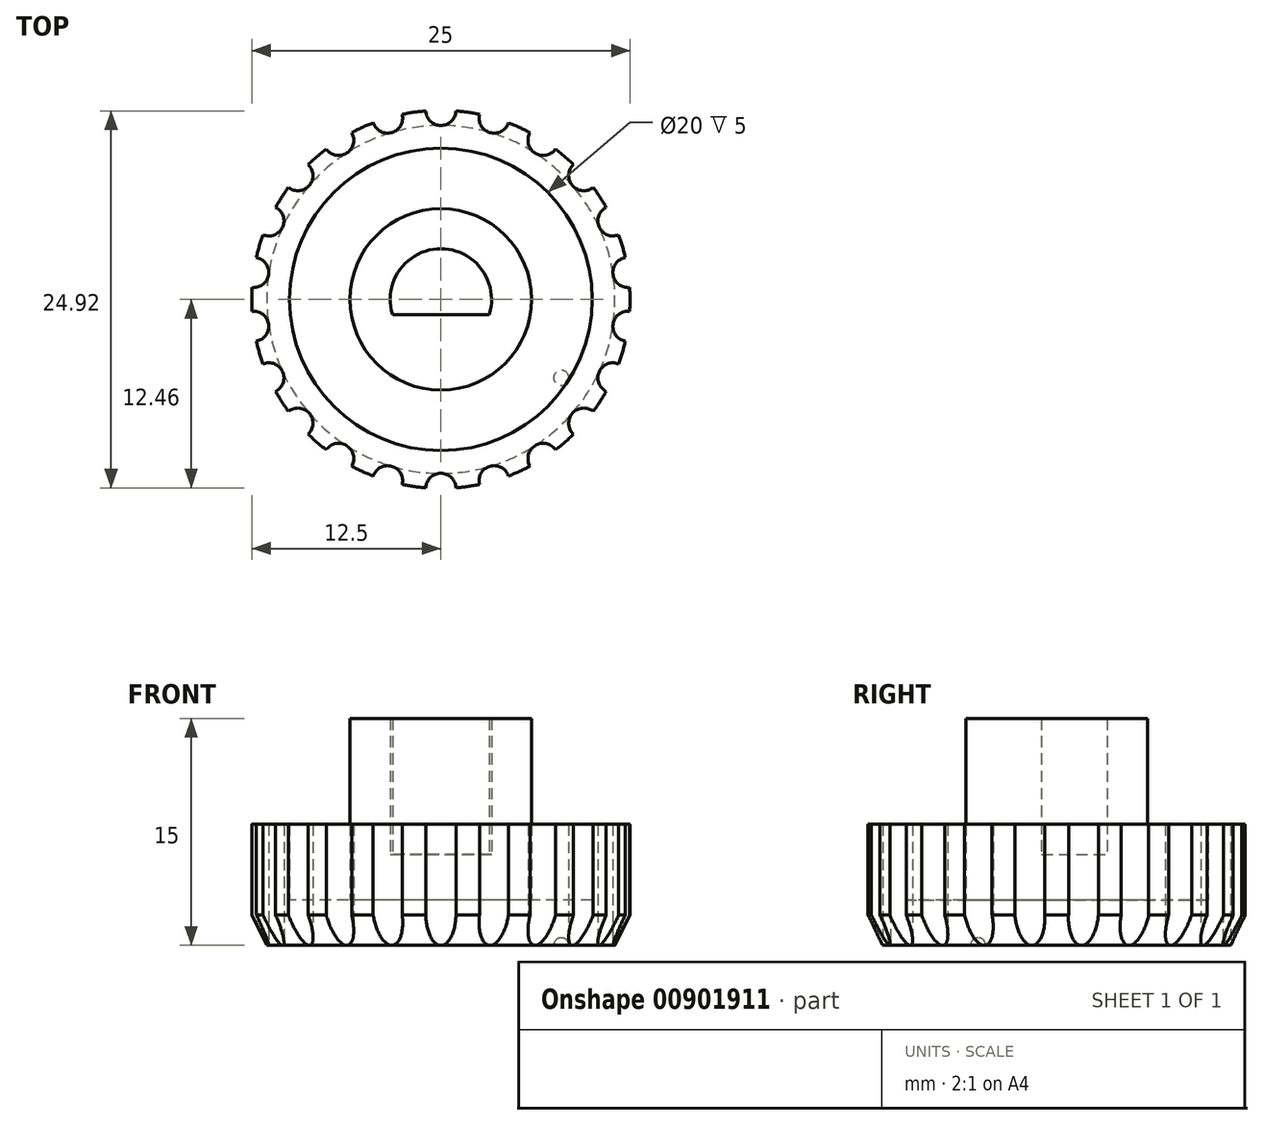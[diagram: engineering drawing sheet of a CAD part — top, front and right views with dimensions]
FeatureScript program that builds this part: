
annotation { "Feature Type Name" : "Feature", "Feature Type Description" : "" }
export const myFeature = defineFeature(function(context is Context, id is Id, definition is map)
    precondition{}
    {
        {
            var Q0;
            Q0=qCreatedBy(makeId("Top.planeOp"),FACE);
            var sketch = newSketch(context, id + "F0", { "sketchPlane" : qUnion([Q0])});
            skCircle(sketch, "E0", {"center": v(0, 0) * mm, "radius": 12.5 * mm});
            skCircle(sketch, "E1", {"center": v(0, 0) * mm, "radius": 6 * mm});
            skArc(sketch, "E2", {"start": v(3.2, -1) * mm, "mid": v(0, 3.35) * mm, "end": v(-3.2, -1) * mm});
            skLineSegment(sketch, "E3", {"start": v(-3.2, -1) * mm, "end": v(3.2, -1) * mm});
            skLineSegment(sketch, "E4", {"start": v(0, 3.35) * mm, "end": v(2.85, 3.35) * mm, "construction": true});
            skCircle(sketch, "E5", {"center": v(0, 0) * mm, "radius": 10 * mm});
            skCircle(sketch, "E6", {"center": v(0, 0) * mm, "radius": 11.5 * mm, "construction": true});
            skArc(sketch, "E7", {"start": v(-1, 12.46) * mm, "mid": v(0, 11.5) * mm, "end": v(1, 12.46) * mm});
            skArc(sketch, "E8.1.0", {"start": v(-4.47, 11.67) * mm, "mid": v(-3.24, 11.03) * mm, "end": v(-2.55, 12.24) * mm});
            skArc(sketch, "E8.2.0", {"start": v(-7.58, 9.94) * mm, "mid": v(-6.22, 9.67) * mm, "end": v(-5.9, 11.02) * mm});
            skArc(sketch, "E8.3.0", {"start": v(-10.07, 7.4) * mm, "mid": v(-8.7, 7.53) * mm, "end": v(-8.76, 8.91) * mm});
            skArc(sketch, "E8.4.0", {"start": v(-11.75, 4.27) * mm, "mid": v(-10.46, 4.78) * mm, "end": v(-10.92, 6.08) * mm});
            skArc(sketch, "E8.5.0", {"start": v(-12.48, 0.78) * mm, "mid": v(-11.38, 1.64) * mm, "end": v(-12.2, 2.76) * mm});
            skArc(sketch, "E8.6.0", {"start": v(-12.2, -2.76) * mm, "mid": v(-11.38, -1.64) * mm, "end": v(-12.48, -0.78) * mm});
            skArc(sketch, "E8.7.0", {"start": v(-10.92, -6.08) * mm, "mid": v(-10.46, -4.78) * mm, "end": v(-11.75, -4.27) * mm});
            skArc(sketch, "E8.8.0", {"start": v(-8.76, -8.91) * mm, "mid": v(-8.7, -7.53) * mm, "end": v(-10.07, -7.4) * mm});
            skArc(sketch, "E8.9.0", {"start": v(-5.9, -11.02) * mm, "mid": v(-6.22, -9.67) * mm, "end": v(-7.58, -9.94) * mm});
            skArc(sketch, "E8.10.0", {"start": v(-2.55, -12.24) * mm, "mid": v(-3.24, -11.03) * mm, "end": v(-4.47, -11.67) * mm});
            skArc(sketch, "E8.11.0", {"start": v(1, -12.46) * mm, "mid": v(0, -11.5) * mm, "end": v(-1, -12.46) * mm});
            skArc(sketch, "E8.12.0", {"start": v(4.47, -11.67) * mm, "mid": v(3.24, -11.03) * mm, "end": v(2.55, -12.24) * mm});
            skArc(sketch, "E8.13.0", {"start": v(7.58, -9.94) * mm, "mid": v(6.22, -9.67) * mm, "end": v(5.9, -11.02) * mm});
            skArc(sketch, "E8.14.0", {"start": v(10.07, -7.4) * mm, "mid": v(8.7, -7.53) * mm, "end": v(8.76, -8.91) * mm});
            skArc(sketch, "E8.15.0", {"start": v(11.75, -4.27) * mm, "mid": v(10.46, -4.78) * mm, "end": v(10.92, -6.08) * mm});
            skArc(sketch, "E8.16.0", {"start": v(12.48, -0.78) * mm, "mid": v(11.38, -1.64) * mm, "end": v(12.2, -2.76) * mm});
            skArc(sketch, "E8.17.0", {"start": v(12.2, 2.76) * mm, "mid": v(11.38, 1.64) * mm, "end": v(12.48, 0.78) * mm});
            skArc(sketch, "E8.18.0", {"start": v(10.92, 6.08) * mm, "mid": v(10.46, 4.78) * mm, "end": v(11.75, 4.27) * mm});
            skArc(sketch, "E8.19.0", {"start": v(8.76, 8.91) * mm, "mid": v(8.7, 7.53) * mm, "end": v(10.07, 7.4) * mm});
            skArc(sketch, "E8.20.0", {"start": v(5.9, 11.02) * mm, "mid": v(6.22, 9.67) * mm, "end": v(7.58, 9.94) * mm});
            skArc(sketch, "E8.21.0", {"start": v(2.55, 12.24) * mm, "mid": v(3.24, 11.03) * mm, "end": v(4.47, 11.67) * mm});
            skCircle(sketch, "E9", {"center": v(7.96, -5.19) * mm, "radius": 0.5 * mm});
            skSolve(sketch);
        }
        {
            var Q0;
            Q0=makeQuery(id+"F0.imprint","IMPRINT",FACE,{"disambiguationData":[TD([[makeQuery(id+"F0.imprint","IMPRINT",EDGE,{"derivedFrom":sQuery(id+"F0.wireOp",EDGE,"E0")}),1.0]])]});
            extrude(context, id + "F1", {"entities" : qUnion([Q0]), "depth" : 8 * mm, "offsetDistance" : 25 * mm});
        }
        {
            var Q0;
            Q0=makeQuery(id+"F0.imprint","IMPRINT",FACE,{"disambiguationData":[TD([[makeQuery(id+"F0.imprint","IMPRINT",EDGE,{"derivedFrom":sQuery(id+"F0.wireOp",EDGE,"E1")}),-1.0]])]});
            var Q1;
            Q1=makeQuery(id+"F0.imprint","IMPRINT",FACE,{"disambiguationData":[TD([[makeQuery(id+"F0.imprint","IMPRINT",EDGE,{"derivedFrom":sQuery(id+"F0.wireOp",EDGE,"E9")}),1.0]])]});
            extrude(context, id + "F2", {"entities" : qUnion([Q0, Q1]), "operationType" : NewBodyOperationType.ADD, "depth" : 3 * mm, "offsetDistance" : 25 * mm});
        }
        {
            var Q0;
            Q0=makeQuery(id+"F0.imprint","IMPRINT",FACE,{"disambiguationData":[TD([[makeQuery(id+"F0.imprint","IMPRINT",EDGE,{"derivedFrom":sQuery(id+"F0.wireOp",EDGE,"E1")}),1.0]])]});
            extrude(context, id + "F3", {"entities" : qUnion([Q0]), "operationType" : NewBodyOperationType.ADD, "depth" : 15 * mm, "offsetDistance" : 25 * mm});
        }
        {
            var Q0;
            Q0=makeQuery(id+"F0.imprint","IMPRINT",FACE,{"disambiguationData":[TD([[makeQuery(id+"F0.imprint","IMPRINT",EDGE,{"derivedFrom":sQuery(id+"F0.wireOp",EDGE,"E2")}),1.0]])]});
            extrude(context, id + "F4", {"entities" : qUnion([Q0]), "operationType" : NewBodyOperationType.ADD, "depth" : 6 * mm, "offsetDistance" : 25 * mm});
        }
        {
            var Q0;
            Q0=qCreatedBy(makeId("Front.planeOp"),FACE);
            var sketch = newSketch(context, id + "F5", { "sketchPlane" : qUnion([Q0])});
            skLineSegment(sketch, "E10", {"start": v(-12.5, 0) * mm, "end": v(-12.5, 2) * mm});
            skLineSegment(sketch, "E11", {"start": v(-12.5, 2) * mm, "end": v(-11.5, 0) * mm});
            skLineSegment(sketch, "E12", {"start": v(-11.5, 0) * mm, "end": v(-12.5, 0) * mm});
            skSolve(sketch);
        }
        {
            var Q0;
            Q0=makeQuery(id+"F5.imprint","IMPRINT",FACE,{"disambiguationData":[TD([[makeQuery(id+"F5.imprint","IMPRINT",EDGE,{"derivedFrom":sQuery(id+"F5.wireOp",EDGE,"E10")}),-1.0]])]});
            var Q1;
            Q1=sQuery(id+"F5.wireOp",EDGE,"E12");
            var Q2;
            Q2=sQuery(id+"F5.wireOp",EDGE,"E10");
            var Q3;
            Q3=sQuery(id+"F5.wireOp",EDGE,"E11");
            var Q4;
            Q4=sQuery(id+"F0.wireOp",EDGE,"E0");
            sweep(context, id + "F6", {"operationType" : NewBodyOperationType.REMOVE, "profiles" : qUnion([Q0]), "surfaceProfiles" : qUnion([Q1, Q2, Q3]), "path" : qUnion([Q4])});
        }
        {
            var Q0;
            Q0=makeQuery(id+"F0.imprint","IMPRINT",FACE,{"disambiguationData":[TD([[makeQuery(id+"F0.imprint","IMPRINT",EDGE,{"derivedFrom":sQuery(id+"F0.wireOp",EDGE,"E9")}),1.0]])]});
            extrude(context, id + "F7", {"entities" : qUnion([Q0]), "operationType" : NewBodyOperationType.REMOVE, "depth" : .5 * mm, "offsetDistance" : 25 * mm});
        }
        {
            var Q0;
            Q0=makeQuery(id+"F7.boolean.opBoolean","COPY",EDGE,{"derivedFrom":makeQuery(id+"F7.opExtrude","CAP_EDGE",EDGE,{"disambiguationData":[OSD([sQuery(id+"F0.wireOp",EDGE,"E9")])],"isStart":false})});
            fillet(context, id + "F8", {"entities" : qUnion([Q0]), "tangentPropagation" : true, "radius" : .5 * mm, "defaultsChanged" : true, "vertexSettings" : [], "allowEdgeOverflow" : false});
        }
    });
